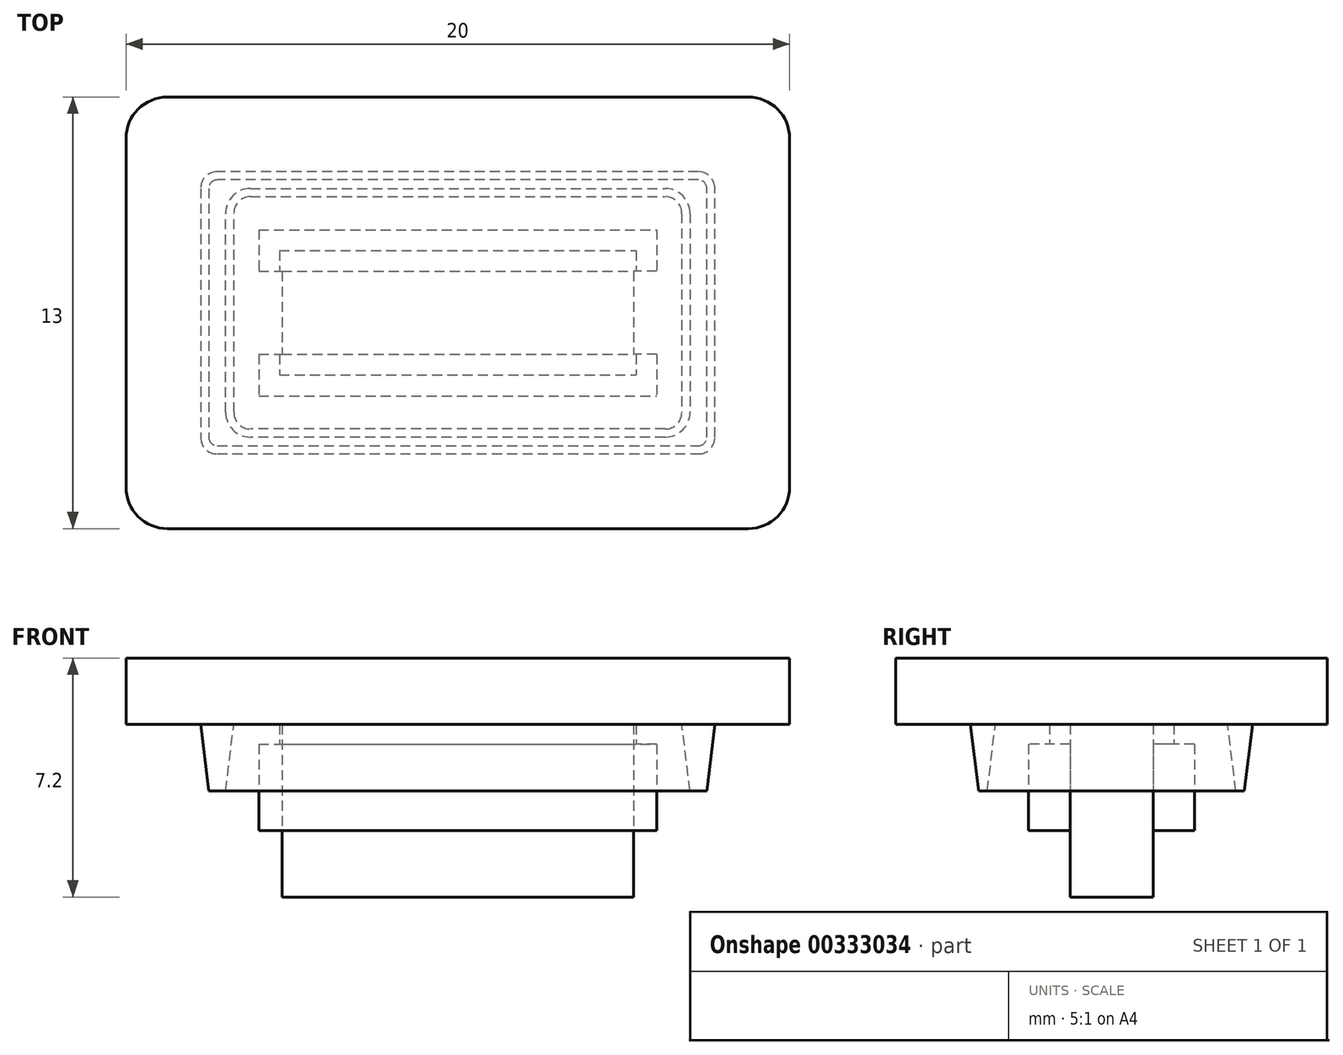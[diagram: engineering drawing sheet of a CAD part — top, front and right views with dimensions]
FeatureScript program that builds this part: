
annotation { "Feature Type Name" : "Feature", "Feature Type Description" : "" }
export const myFeature = defineFeature(function(context is Context, id is Id, definition is map)
    precondition{}
    {
        {
            var Q0;
            Q0=qCreatedBy(makeId("Top.planeOp"),FACE);
            var sketch = newSketch(context, id + "F0", { "sketchPlane" : qUnion([Q0])});
            skLineSegment(sketch, "E0.bottom", {"start": v(-6, 2.5) * mm, "end": v(6, 2.5) * mm});
            skLineSegment(sketch, "E0.top", {"start": v(-6, -2.5) * mm, "end": v(6, -2.5) * mm});
            skLineSegment(sketch, "E0.left", {"start": v(-6, 2.5) * mm, "end": v(-6, -2.5) * mm});
            skLineSegment(sketch, "E0.right", {"start": v(6, 2.5) * mm, "end": v(6, -2.5) * mm});
            skPoint(sketch, "E0.middle", {"position": v(0, 0) * mm});
            skLineSegment(sketch, "E1.bottom", {"start": v(-6, 1.25) * mm, "end": v(-5.3, 1.25) * mm});
            skLineSegment(sketch, "E1.top", {"start": v(-6, -1.25) * mm, "end": v(-5.3, -1.25) * mm});
            skLineSegment(sketch, "E1.left", {"start": v(-6, 1.25) * mm, "end": v(-6, -1.25) * mm});
            skLineSegment(sketch, "E1.right", {"start": v(-5.3, 1.25) * mm, "end": v(-5.3, -1.25) * mm});
            skLineSegment(sketch, "E2.MirrorCS", {"start": v(5.3, 1.25) * mm, "end": v(5.3, -1.25) * mm});
            skLineSegment(sketch, "E3.MirrorCS", {"start": v(6, 1.25) * mm, "end": v(6, -1.25) * mm});
            skLineSegment(sketch, "E4.MirrorCS", {"start": v(6, -1.25) * mm, "end": v(5.3, -1.25) * mm});
            skLineSegment(sketch, "E5.MirrorCS", {"start": v(6, 1.25) * mm, "end": v(5.3, 1.25) * mm});
            skSolve(sketch);
        }
        {
            var Q0;
            {var subQ6=sQuery(id+"F0.wireOp",EDGE,"E0.bottom");Q0=makeQuery(id+"F0.imprint","IMPRINT",FACE,{"disambiguationData":[TD([[makeQuery(id+"F0.imprint","IMPRINT",EDGE,{"derivedFrom":subQ6}),-1.0]])]});}
            extrude(context, id + "F1", {"entities" : qUnion([Q0]), "depth" : 2.6 * mm});
        }
        {
            var Q0;
            Q0=makeQuery(id+"F1.opExtrude","CAP_FACE",FACE,{"disambiguationData":[OSD([sQuery(id+"F0.wireOp",EDGE,"E0.bottom"),sQuery(id+"F0.wireOp",EDGE,"E0.top"),sQuery(id+"F0.wireOp",EDGE,"E0.left"),sQuery(id+"F0.wireOp",EDGE,"E0.right"),sQuery(id+"F0.wireOp",EDGE,"E1.bottom"),sQuery(id+"F0.wireOp",EDGE,"E1.top"),sQuery(id+"F0.wireOp",EDGE,"E1.right"),sQuery(id+"F0.wireOp",EDGE,"E2.MirrorCS"),sQuery(id+"F0.wireOp",EDGE,"E4.MirrorCS"),sQuery(id+"F0.wireOp",EDGE,"E5.MirrorCS")])],"isStart":true});
            var sketch = newSketch(context, id + "F2", { "sketchPlane" : qUnion([Q0])});
            skLineSegment(sketch, "E6.bottom", {"start": v(-5.3, 1.25) * mm, "end": v(5.3, 1.25) * mm});
            skLineSegment(sketch, "E6.top", {"start": v(-5.3, -1.25) * mm, "end": v(5.3, -1.25) * mm});
            skLineSegment(sketch, "E6.left", {"start": v(-5.3, 1.25) * mm, "end": v(-5.3, -1.25) * mm});
            skLineSegment(sketch, "E6.right", {"start": v(5.3, 1.25) * mm, "end": v(5.3, -1.25) * mm});
            skSolve(sketch);
        }
        {
            var Q0;
            Q0 = qSketchRegion(id + "F2", true);
            extrude(context, id + "F3", {"entities" : qUnion([Q0]), "operationType" : NewBodyOperationType.ADD, "depth" : 2 * mm});
        }
        {
            var Q0;
            Q0=makeQuery(id+"F1.opExtrude","CAP_FACE",FACE,{"disambiguationData":[OSD([sQuery(id+"F0.wireOp",EDGE,"E0.bottom"),sQuery(id+"F0.wireOp",EDGE,"E0.top"),sQuery(id+"F0.wireOp",EDGE,"E0.left"),sQuery(id+"F0.wireOp",EDGE,"E0.right"),sQuery(id+"F0.wireOp",EDGE,"E1.bottom"),sQuery(id+"F0.wireOp",EDGE,"E1.top"),sQuery(id+"F0.wireOp",EDGE,"E1.right"),sQuery(id+"F0.wireOp",EDGE,"E2.MirrorCS"),sQuery(id+"F0.wireOp",EDGE,"E4.MirrorCS"),sQuery(id+"F0.wireOp",EDGE,"E5.MirrorCS")])],"isStart":false});
            var sketch = newSketch(context, id + "F4", { "sketchPlane" : qUnion([Q0])});
            skLineSegment(sketch, "E7.bottom", {"start": v(-5.37, 1.87) * mm, "end": v(5.37, 1.87) * mm});
            skLineSegment(sketch, "E7.top", {"start": v(-5.37, -1.87) * mm, "end": v(5.37, -1.87) * mm});
            skLineSegment(sketch, "E7.left", {"start": v(-5.37, 1.87) * mm, "end": v(-5.37, -1.87) * mm});
            skLineSegment(sketch, "E7.right", {"start": v(5.37, 1.87) * mm, "end": v(5.37, -1.87) * mm});
            skPoint(sketch, "E7.middle", {"position": v(0, 0) * mm});
            skSolve(sketch);
        }
        {
            var Q0;
            {var subQ15=sQuery(id+"F4.wireOp",EDGE,"ptJB8pNf-NBoq-jo5t-yNir-1qXlF4JjkNrf.bottom");Q0=makeQuery(id+"F4.imprint","IMPRINT",FACE,{"disambiguationData":[TD([[makeQuery(id+"F4.imprint","IMPRINT",EDGE,{"derivedFrom":subQ15}),-1.0]])]});}
            var Q1;
            {var subQ10=sQuery(id+"F4.wireOp",EDGE,"E7.bottom");Q1=makeQuery(id+"F4.imprint","IMPRINT",FACE,{"disambiguationData":[TD([[makeQuery(id+"F4.imprint","IMPRINT",EDGE,{"derivedFrom":subQ10}),-1.0]])]});}
            extrude(context, id + "F5", {"entities" : qUnion([Q0, Q1]), "operationType" : NewBodyOperationType.ADD, "depth" : .6 * mm});
        }
        {
            var Q0;
            Q0=makeQuery(id+"F5.opExtrude","CAP_FACE",FACE,{"disambiguationData":[OSD([sQuery(id+"F0.wireOp",EDGE,"E1.bottom"),sQuery(id+"F0.wireOp",EDGE,"E1.top"),sQuery(id+"F0.wireOp",EDGE,"E1.right"),sQuery(id+"F0.wireOp",EDGE,"E2.MirrorCS"),sQuery(id+"F0.wireOp",EDGE,"E4.MirrorCS"),sQuery(id+"F0.wireOp",EDGE,"E5.MirrorCS"),sQuery(id+"F4.wireOp",EDGE,"E7.bottom"),sQuery(id+"F4.wireOp",EDGE,"E7.top"),sQuery(id+"F4.wireOp",EDGE,"E7.left"),sQuery(id+"F4.wireOp",EDGE,"E7.right")])],"isStart":false});
            var sketch = newSketch(context, id + "F6", { "sketchPlane" : qUnion([Q0])});
            skLineSegment(sketch, "E8.bottom", {"start": v(-8.75, 6.5) * mm, "end": v(8.75, 6.5) * mm});
            skLineSegment(sketch, "E8.top", {"start": v(-8.75, -6.5) * mm, "end": v(8.75, -6.5) * mm});
            skLineSegment(sketch, "E8.left", {"start": v(-10, 5.25) * mm, "end": v(-10, -5.25) * mm});
            skLineSegment(sketch, "E8.right", {"start": v(10, 5.25) * mm, "end": v(10, -5.25) * mm});
            skPoint(sketch, "E8.middle", {"position": v(0, 0) * mm});
            skPoint(sketch, "E9.visualSharp", {"position": v(-10, -6.5) * mm});
            skArc(sketch, "E9.filletArc", {"start": v(-10, -5.25) * mm, "mid": v(-9.63, -6.13) * mm, "end": v(-8.75, -6.5) * mm});
            skPoint(sketch, "E10.visualSharp", {"position": v(10, -6.5) * mm});
            skArc(sketch, "E10.filletArc", {"start": v(8.75, -6.5) * mm, "mid": v(9.63, -6.13) * mm, "end": v(10, -5.25) * mm});
            skPoint(sketch, "E11.visualSharp", {"position": v(10, 6.5) * mm});
            skArc(sketch, "E11.filletArc", {"start": v(10, 5.25) * mm, "mid": v(9.63, 6.13) * mm, "end": v(8.75, 6.5) * mm});
            skPoint(sketch, "E12.visualSharp", {"position": v(-10, 6.5) * mm});
            skArc(sketch, "E12.filletArc", {"start": v(-8.75, 6.5) * mm, "mid": v(-9.63, 6.13) * mm, "end": v(-10, 5.25) * mm});
            skSolve(sketch);
        }
        {
            var Q0;
            Q0 = qSketchRegion(id + "F6", true);
            extrude(context, id + "F7", {"entities" : qUnion([Q0]), "operationType" : NewBodyOperationType.ADD, "depth" : 2 * mm});
        }
        {
            var Q0;
            Q0=makeQuery(id+"F7.opExtrude","CAP_FACE",FACE,{"disambiguationData":[OSD([sQuery(id+"F6.wireOp",EDGE,"E8.bottom"),sQuery(id+"F6.wireOp",EDGE,"E8.top"),sQuery(id+"F6.wireOp",EDGE,"E8.left"),sQuery(id+"F6.wireOp",EDGE,"E8.right"),sQuery(id+"F6.wireOp",EDGE,"E9.filletArc"),sQuery(id+"F6.wireOp",EDGE,"E10.filletArc"),sQuery(id+"F6.wireOp",EDGE,"E11.filletArc"),sQuery(id+"F6.wireOp",EDGE,"E12.filletArc")])],"isStart":true});
            var sketch = newSketch(context, id + "F8", { "sketchPlane" : qUnion([Q0])});
            skLineSegment(sketch, "E13.bottom", {"start": v(-6.25, 3.5) * mm, "end": v(6.25, 3.5) * mm});
            skLineSegment(sketch, "E13.top", {"start": v(-6.25, -3.5) * mm, "end": v(6.25, -3.5) * mm});
            skLineSegment(sketch, "E13.left", {"start": v(-6.75, 3) * mm, "end": v(-6.75, -3) * mm});
            skLineSegment(sketch, "E13.right", {"start": v(6.75, 3) * mm, "end": v(6.75, -3) * mm});
            skPoint(sketch, "E13.middle", {"position": v(0, 0) * mm});
            skLineSegment(sketch, "E14.bottom", {"start": v(-7.25, 4.25) * mm, "end": v(7.25, 4.25) * mm});
            skLineSegment(sketch, "E14.top", {"start": v(-7.25, -4.25) * mm, "end": v(7.25, -4.25) * mm});
            skLineSegment(sketch, "E14.left", {"start": v(-7.75, 3.75) * mm, "end": v(-7.75, -3.75) * mm});
            skLineSegment(sketch, "E14.right", {"start": v(7.75, 3.75) * mm, "end": v(7.75, -3.75) * mm});
            skPoint(sketch, "E15.visualSharp", {"position": v(-6.75, 3.5) * mm});
            skArc(sketch, "E15.filletArc", {"start": v(-6.25, 3.5) * mm, "mid": v(-6.6, 3.35) * mm, "end": v(-6.75, 3) * mm});
            skPoint(sketch, "E16.visualSharp", {"position": v(6.75, 3.5) * mm});
            skArc(sketch, "E16.filletArc", {"start": v(6.75, 3) * mm, "mid": v(6.6, 3.35) * mm, "end": v(6.25, 3.5) * mm});
            skPoint(sketch, "E17.visualSharp", {"position": v(6.75, -3.5) * mm});
            skArc(sketch, "E17.filletArc", {"start": v(6.25, -3.5) * mm, "mid": v(6.6, -3.35) * mm, "end": v(6.75, -3) * mm});
            skPoint(sketch, "E18.visualSharp", {"position": v(-6.75, -3.5) * mm});
            skArc(sketch, "E18.filletArc", {"start": v(-6.75, -3) * mm, "mid": v(-6.6, -3.35) * mm, "end": v(-6.25, -3.5) * mm});
            skPoint(sketch, "E19.visualSharp", {"position": v(-7.75, 4.25) * mm});
            skArc(sketch, "E19.filletArc", {"start": v(-7.25, 4.25) * mm, "mid": v(-7.6, 4.1) * mm, "end": v(-7.75, 3.75) * mm});
            skPoint(sketch, "E20.visualSharp", {"position": v(7.75, 4.25) * mm});
            skArc(sketch, "E20.filletArc", {"start": v(7.75, 3.75) * mm, "mid": v(7.6, 4.1) * mm, "end": v(7.25, 4.25) * mm});
            skPoint(sketch, "E21.visualSharp", {"position": v(7.75, -4.25) * mm});
            skArc(sketch, "E21.filletArc", {"start": v(7.25, -4.25) * mm, "mid": v(7.6, -4.1) * mm, "end": v(7.75, -3.75) * mm});
            skPoint(sketch, "E22.visualSharp", {"position": v(-7.75, -4.25) * mm});
            skArc(sketch, "E22.filletArc", {"start": v(-7.75, -3.75) * mm, "mid": v(-7.6, -4.1) * mm, "end": v(-7.25, -4.25) * mm});
            skSolve(sketch);
        }
        {
            var Q0;
            Q0 = qSketchRegion(id + "F8", true);
            extrude(context, id + "F9", {"entities" : qUnion([Q0]), "operationType" : NewBodyOperationType.ADD, "depth" : 2 * mm, "hasDraft" : true, "draftAngle" : 7 * degree, "draftPullDirection" : true});
        }
    });
